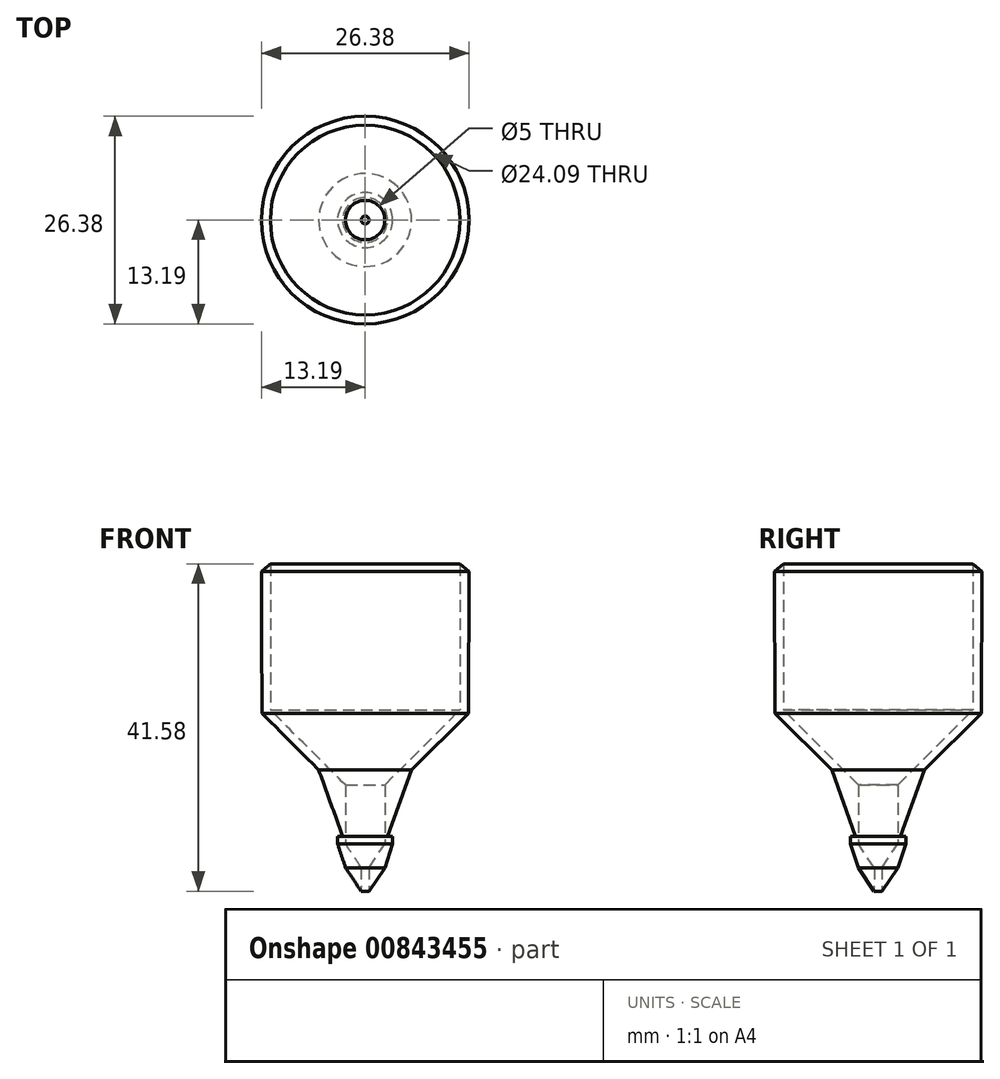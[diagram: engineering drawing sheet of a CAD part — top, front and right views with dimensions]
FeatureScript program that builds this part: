
annotation { "Feature Type Name" : "Feature", "Feature Type Description" : "" }
export const myFeature = defineFeature(function(context is Context, id is Id, definition is map)
    precondition{}
    {
        {
            var Q0;
            Q0=qCreatedBy(makeId("Front.planeOp"),FACE);
            var sketch = newSketch(context, id + "F0", { "sketchPlane" : qUnion([Q0])});
            skLineSegment(sketch, "E0", {"start": v(0, 0) * mm, "end": v(0, 1.5) * mm});
            skLineSegment(sketch, "E1", {"start": v(0, 0) * mm, "end": v(-10.6, 10.6) * mm});
            skLineSegment(sketch, "E2", {"start": v(2.5, -12.43) * mm, "end": v(2.5, 47.57) * mm});
            skLineSegment(sketch, "E3", {"start": v(0, 1.5) * mm, "end": v(-9.55, 11.05) * mm});
            skLineSegment(sketch, "E4", {"start": v(-10.6, 10.6) * mm, "end": v(-10.69, 28.6) * mm});
            skLineSegment(sketch, "E5", {"start": v(-10.69, 28.6) * mm, "end": v(-9.55, 29.58) * mm});
            skLineSegment(sketch, "E6", {"start": v(0, 0) * mm, "end": v(0, -6) * mm});
            skLineSegment(sketch, "E7", {"start": v(0, -6) * mm, "end": v(-3.4, 3.4) * mm});
            skLineSegment(sketch, "E8.bottom", {"start": v(0, -6) * mm, "end": v(-1, -6) * mm});
            skLineSegment(sketch, "E8.top", {"start": v(0, -5) * mm, "end": v(-1, -5) * mm});
            skLineSegment(sketch, "E8.left", {"start": v(0, -6) * mm, "end": v(0, -5) * mm});
            skLineSegment(sketch, "E8.right", {"start": v(-1, -6) * mm, "end": v(-1, -5) * mm});
            skLineSegment(sketch, "E9", {"start": v(0, -6) * mm, "end": v(0, -9) * mm});
            skLineSegment(sketch, "E10", {"start": v(-1, -6) * mm, "end": v(0, -9) * mm});
            skLineSegment(sketch, "E11", {"start": v(0, -6) * mm, "end": v(2, -9) * mm});
            skLineSegment(sketch, "E12", {"start": v(2, -9) * mm, "end": v(0, -9) * mm});
            skLineSegment(sketch, "E13", {"start": v(0, -9) * mm, "end": v(2, -12) * mm});
            skLineSegment(sketch, "E14", {"start": v(2, -12) * mm, "end": v(2, -9) * mm});
            skLineSegment(sketch, "E15", {"start": v(-9.55, 29.58) * mm, "end": v(-9.55, 11.05) * mm});
            skSolve(sketch);
        }
        {
            var Q0;
            Q0 = qSketchRegion(id + "F0", true);
            var Q1;
            Q1=sQuery(id+"F0.wireOp",EDGE,"E2");
            revolve(context, id + "F1", {"surfaceOperationType" : NewSurfaceOperationType.NEW, "entities" : qUnion([Q0]), "axis" : qUnion([Q1]), "revolveType" : RevolveType.ONE_DIRECTION, "angle" : 360 * degree});
        }
    });
